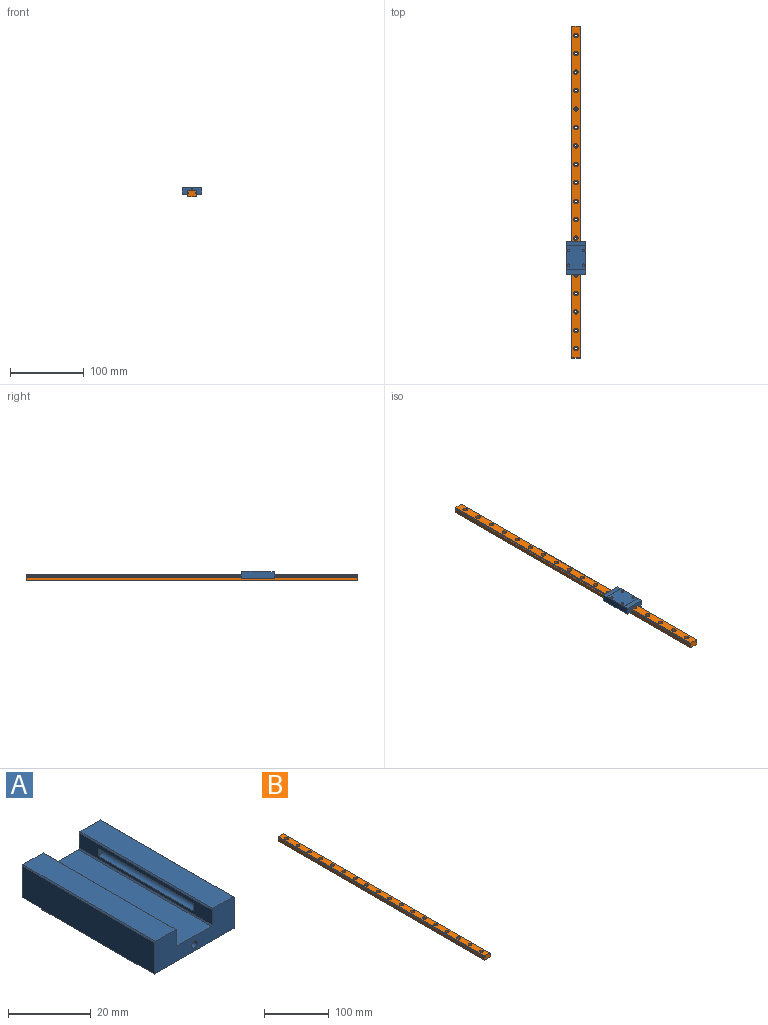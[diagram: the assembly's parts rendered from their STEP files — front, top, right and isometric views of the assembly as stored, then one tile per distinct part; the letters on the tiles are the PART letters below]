
ASSEMBLY  parts=2 mates=1
PART A: 37 faces, bbox 27x45.4x10 mm
  f0: plane 45.4x0.3mm, normal (-0.71,0,0.71), area 19.3mm2, adj f3,f6,f22,f23
  f1: plane 45.4x0.3mm, normal (0.71,0,0.71), area 19.3mm2, adj f10,f11,f22,f23
  f2: plane 45.4x0.3mm, normal (0.71,0,0.71), area 19.3mm2, adj f6,f7,f22,f23
  f3: plane 45.4x4.4mm, normal (-1,0,0), area 129.2mm2, adj f0,f5,f17,f20,f22,f23,f24
  f4: plane 45.4x11.4mm, normal (0,0,1), area 517.6mm2, adj f16,f17,f22,f23
  f5: cylinder r=1.15mm len=32.4mm, axis (0,-1,0), area 141.5mm2, adj f3,f20,f24
  f6: plane 45.4x6.9mm, normal (0,0,1), area 313.3mm2, adj f0,f2,f22,f23
  f7: plane 45.4x9.4mm, normal (1,0,0), area 424.2mm2, adj f2,f15,f18,f21,f22,f23,f25,f35
  f8: plane 32.4x26.4mm, normal (0,0,-1), area 821.1mm2, adj f14,f15,f18,f27,f29,f31,f33,f35
  f9: plane 45.4x9.4mm, normal (-1,0,0), area 424.2mm2, adj f14,f18,f21,f22,f23,f25,f34,f35
  f10: plane 45.4x6.9mm, normal (0,0,1), area 313.3mm2, adj f1,f22,f23,f34
  f11: plane 45.4x4.4mm, normal (1,0,0), area 129.2mm2, adj f1,f12,f16,f19,f22,f23,f36
  f12: cylinder r=1.15mm len=32.4mm, axis (0,-1,0), area 141.5mm2, adj f11,f19,f36
  f13: cylinder r=1mm len=45.4mm, axis (0,-1,0), area 285.3mm2, adj f22,f23
  f14: plane 32.4x0.3mm, normal (-0.71,0,-0.71), area 13.7mm2, adj f8,f9,f18,f35
  f15: plane 32.4x0.3mm, normal (0.71,0,-0.71), area 13.7mm2, adj f7,f8,f18,f35
  f16: plane 45.4x0.3mm, normal (0.71,0,0.71), area 19.3mm2, adj f4,f11,f22,f23
  f17: plane 45.4x0.3mm, normal (-0.71,0,0.71), area 19.3mm2, adj f3,f4,f22,f23
  f18: plane 27x0.5mm, normal (0,-1,0), area 13.4mm2, adj f7,f8,f9,f14,f15,f21
  f19: plane 2.3x1.52mm, normal (0,1,0), area 2.9mm2, adj f11,f12
  f20: plane 2.3x1.52mm, normal (0,1,0), area 2.9mm2, adj f3,f5
  f21: plane 27x6.5mm, normal (0,0,-1), area 175.5mm2, adj f7,f9,f18,f22
  f22: plane 27x9.5mm, normal (0,-1,0), area 193.3mm2, adj f0,f1,f2,f3,f4,f6,f7,f9
  f23: plane 27x9.5mm, normal (0,1,0), area 193.3mm2, adj f0,f1,f2,f3,f4,f6,f7,f9
  f24: plane 2.3x1.52mm, normal (0,-1,0), area 2.9mm2, adj f3,f5
  f25: plane 27x6.5mm, normal (0,0,-1), area 175.5mm2, adj f7,f9,f23,f35
  f26: cone r=857.17mm half-angle=59deg, axis (0,0,-1), area 10mm2, adj f27
  f27: cylinder r=1.65mm len=3.5mm, axis (0,0,1), area 36.3mm2, adj f8,f26
  f28: cone r=857.17mm half-angle=59deg, axis (0,0,-1), area 10mm2, adj f29
  f29: cylinder r=1.65mm len=3.5mm, axis (0,0,1), area 36.3mm2, adj f8,f28
  f30: cone r=857.17mm half-angle=59deg, axis (0,0,-1), area 10mm2, adj f31
  f31: cylinder r=1.65mm len=3.5mm, axis (0,0,1), area 36.3mm2, adj f8,f30
  f32: cone r=857.17mm half-angle=59deg, axis (0,0,-1), area 10mm2, adj f33
  f33: cylinder r=1.65mm len=3.5mm, axis (0,0,1), area 36.3mm2, adj f8,f32
  f34: plane 45.4x0.3mm, normal (-0.71,0,0.71), area 19.3mm2, adj f9,f10,f22,f23
  f35: plane 27x0.5mm, normal (0,1,0), area 13.4mm2, adj f7,f8,f9,f14,f15,f25
  f36: plane 2.3x1.52mm, normal (0,-1,0), area 2.9mm2, adj f11,f12
PART B: 76 faces, bbox 12x450x8 mm
  f0: plane 450x0.51mm, normal (0,0,1), area 229.4mm2, adj f1,f19,f20,f51
  f1: plane 450x0.3mm, normal (1,0,0), area 135mm2, adj f0,f2,f20,f51
  f2: plane 450x0.51mm, normal (0,0,-1), area 229.4mm2, adj f1,f3,f20,f51
  f3: cylinder r=1.15mm len=450mm, axis (0,1,0), area 575.7mm2, adj f2,f4,f20,f51
  f4: plane 450x0.86mm, normal (1,0,0), area 387.4mm2, adj f3,f5,f20,f51
  f5: plane 450x0.35mm, normal (0.71,0,0.71), area 222.7mm2, adj f4,f6,f20,f51
  f6: plane 450x11.3mm, normal (0,0,1), area 4576.1mm2, adj f5,f7,f20,f23,f26,f29,f32,f35
  f7: plane 450x0.35mm, normal (-0.71,0,0.71), area 222.7mm2, adj f6,f8,f20,f51
  f8: plane 450x0.86mm, normal (-1,0,0), area 387.4mm2, adj f7,f9,f20,f51
  f9: cylinder r=1.15mm len=450mm, axis (0,1,0), area 575.7mm2, adj f8,f10,f20,f51
  f10: plane 450x0.51mm, normal (0,0,-1), area 229.4mm2, adj f9,f11,f20,f51
  f11: plane 450x0.3mm, normal (-1,0,0), area 135mm2, adj f10,f12,f20,f51
  f12: plane 450x0.51mm, normal (0,0,1), area 229.4mm2, adj f11,f13,f20,f51
  f13: cylinder r=1.15mm len=450mm, axis (0,1,0), area 575.7mm2, adj f12,f14,f20,f51
  f14: plane 450x4.26mm, normal (-1,0,0), area 1917.6mm2, adj f13,f15,f20,f51
  f15: plane 450x0.35mm, normal (-0.71,0,-0.71), area 222.7mm2, adj f14,f16,f20,f51
  f16: plane 450x11.3mm, normal (0,0,-1), area 4911.8mm2, adj f15,f17,f20,f21,f24,f27,f30,f33
  f17: plane 450x0.35mm, normal (0.71,0,-0.71), area 222.7mm2, adj f16,f18,f20,f51
  f18: plane 450x4.26mm, normal (1,0,0), area 1917.6mm2, adj f17,f19,f20,f51
  f19: cylinder r=1.15mm len=450mm, axis (0,1,0), area 575.7mm2, adj f0,f18,f20,f51
  f20: plane 12x8mm, normal (0,-1,0), area 93mm2, adj f0,f1,f2,f3,f4,f5,f6,f7
  f21: cylinder r=1.75mm len=3.5mm, axis (0,0,1), area 38.5mm2, adj f16,f22
  f22: plane 6x6mm, normal (0,0,1), area 18.7mm2, adj f21,f23
  f23: cylinder r=3mm len=6mm, axis (0,0,1), area 84.8mm2, adj f6,f22
  f24: cylinder r=1.75mm len=3.5mm, axis (0,0,1), area 38.5mm2, adj f16,f25
  f25: plane 6x6mm, normal (0,0,1), area 18.7mm2, adj f24,f26
  f26: cylinder r=3mm len=6mm, axis (0,0,1), area 84.8mm2, adj f6,f25
  f27: cylinder r=1.75mm len=3.5mm, axis (0,0,1), area 38.5mm2, adj f16,f28
  f28: plane 6x6mm, normal (0,0,1), area 18.7mm2, adj f27,f29
  f29: cylinder r=3mm len=6mm, axis (0,0,1), area 84.8mm2, adj f6,f28
  f30: cylinder r=1.75mm len=3.5mm, axis (0,0,1), area 38.5mm2, adj f16,f31
  f31: plane 6x6mm, normal (0,0,1), area 18.7mm2, adj f30,f32
  f32: cylinder r=3mm len=6mm, axis (0,0,1), area 84.8mm2, adj f6,f31
  f33: cylinder r=1.75mm len=3.5mm, axis (0,0,1), area 38.5mm2, adj f16,f34
  f34: plane 6x6mm, normal (0,0,1), area 18.7mm2, adj f33,f35
  f35: cylinder r=3mm len=6mm, axis (0,0,1), area 84.8mm2, adj f6,f34
  f36: cylinder r=1.75mm len=3.5mm, axis (0,0,1), area 38.5mm2, adj f16,f37
  f37: plane 6x6mm, normal (0,0,1), area 18.7mm2, adj f36,f38
  f38: cylinder r=3mm len=6mm, axis (0,0,1), area 84.8mm2, adj f6,f37
  f39: cylinder r=1.75mm len=3.5mm, axis (0,0,1), area 38.5mm2, adj f16,f40
  f40: plane 6x6mm, normal (0,0,1), area 18.7mm2, adj f39,f41
  f41: cylinder r=3mm len=6mm, axis (0,0,1), area 84.8mm2, adj f6,f40
  f42: cylinder r=1.75mm len=3.5mm, axis (0,0,1), area 38.5mm2, adj f16,f43
  f43: plane 6x6mm, normal (0,0,1), area 18.7mm2, adj f42,f44
  f44: cylinder r=3mm len=6mm, axis (0,0,1), area 84.8mm2, adj f6,f43
  f45: cylinder r=1.75mm len=3.5mm, axis (0,0,1), area 38.5mm2, adj f16,f46
  f46: plane 6x6mm, normal (0,0,1), area 18.7mm2, adj f45,f47
  f47: cylinder r=3mm len=6mm, axis (0,0,1), area 84.8mm2, adj f6,f46
  f48: cylinder r=1.75mm len=3.5mm, axis (0,0,1), area 38.5mm2, adj f16,f49
  f49: plane 6x6mm, normal (0,0,1), area 18.7mm2, adj f48,f50
  f50: cylinder r=3mm len=6mm, axis (0,0,1), area 84.8mm2, adj f6,f49
  f51: plane 12x8mm, normal (0,1,0), area 93mm2, adj f0,f1,f2,f3,f4,f5,f6,f7
  f52: cylinder r=1.75mm len=3.5mm, axis (0,0,1), area 38.5mm2, adj f16,f53
  f53: plane 6x6mm, normal (0,0,1), area 18.7mm2, adj f52,f54
  f54: cylinder r=3mm len=6mm, axis (0,0,1), area 84.8mm2, adj f6,f53
  f55: cylinder r=1.75mm len=3.5mm, axis (0,0,1), area 38.5mm2, adj f16,f56
  f56: plane 6x6mm, normal (0,0,1), area 18.7mm2, adj f55,f57
  f57: cylinder r=3mm len=6mm, axis (0,0,1), area 84.8mm2, adj f6,f56
  f58: cylinder r=1.75mm len=3.5mm, axis (0,0,1), area 38.5mm2, adj f16,f59
  f59: plane 6x6mm, normal (0,0,1), area 18.7mm2, adj f58,f60
  f60: cylinder r=3mm len=6mm, axis (0,0,1), area 84.8mm2, adj f6,f59
  f61: cylinder r=1.75mm len=3.5mm, axis (0,0,1), area 38.5mm2, adj f16,f62
  f62: plane 6x6mm, normal (0,0,1), area 18.7mm2, adj f61,f63
  f63: cylinder r=3mm len=6mm, axis (0,0,1), area 84.8mm2, adj f6,f62
  f64: cylinder r=1.75mm len=3.5mm, axis (0,0,1), area 38.5mm2, adj f16,f65
  f65: plane 6x6mm, normal (0,0,1), area 18.7mm2, adj f64,f66
  f66: cylinder r=3mm len=6mm, axis (0,0,1), area 84.8mm2, adj f6,f65
  f67: cylinder r=1.75mm len=3.5mm, axis (0,0,1), area 38.5mm2, adj f16,f68
  f68: plane 6x6mm, normal (0,0,1), area 18.7mm2, adj f67,f69
  f69: cylinder r=3mm len=6mm, axis (0,0,1), area 84.8mm2, adj f6,f68
  f70: cylinder r=1.75mm len=3.5mm, axis (0,0,1), area 38.5mm2, adj f16,f71
  f71: plane 6x6mm, normal (0,0,1), area 18.7mm2, adj f70,f72
  f72: cylinder r=3mm len=6mm, axis (0,0,1), area 84.8mm2, adj f6,f71
  f73: cylinder r=1.75mm len=3.5mm, axis (0,0,1), area 38.5mm2, adj f16,f74
  f74: plane 6x6mm, normal (0,0,1), area 18.7mm2, adj f73,f75
  f75: cylinder r=3mm len=6mm, axis (0,0,1), area 84.8mm2, adj f6,f74
PLACE A rot(axis=(0,1,0),180deg) t=(-21.94,170.03,34.11)mm
PLACE B t=(-21.94,43,34.11)mm
MATE slider B.f20 <-> A.f22  axis (0,-1,0) through (-21.94,18,34.11)mm
